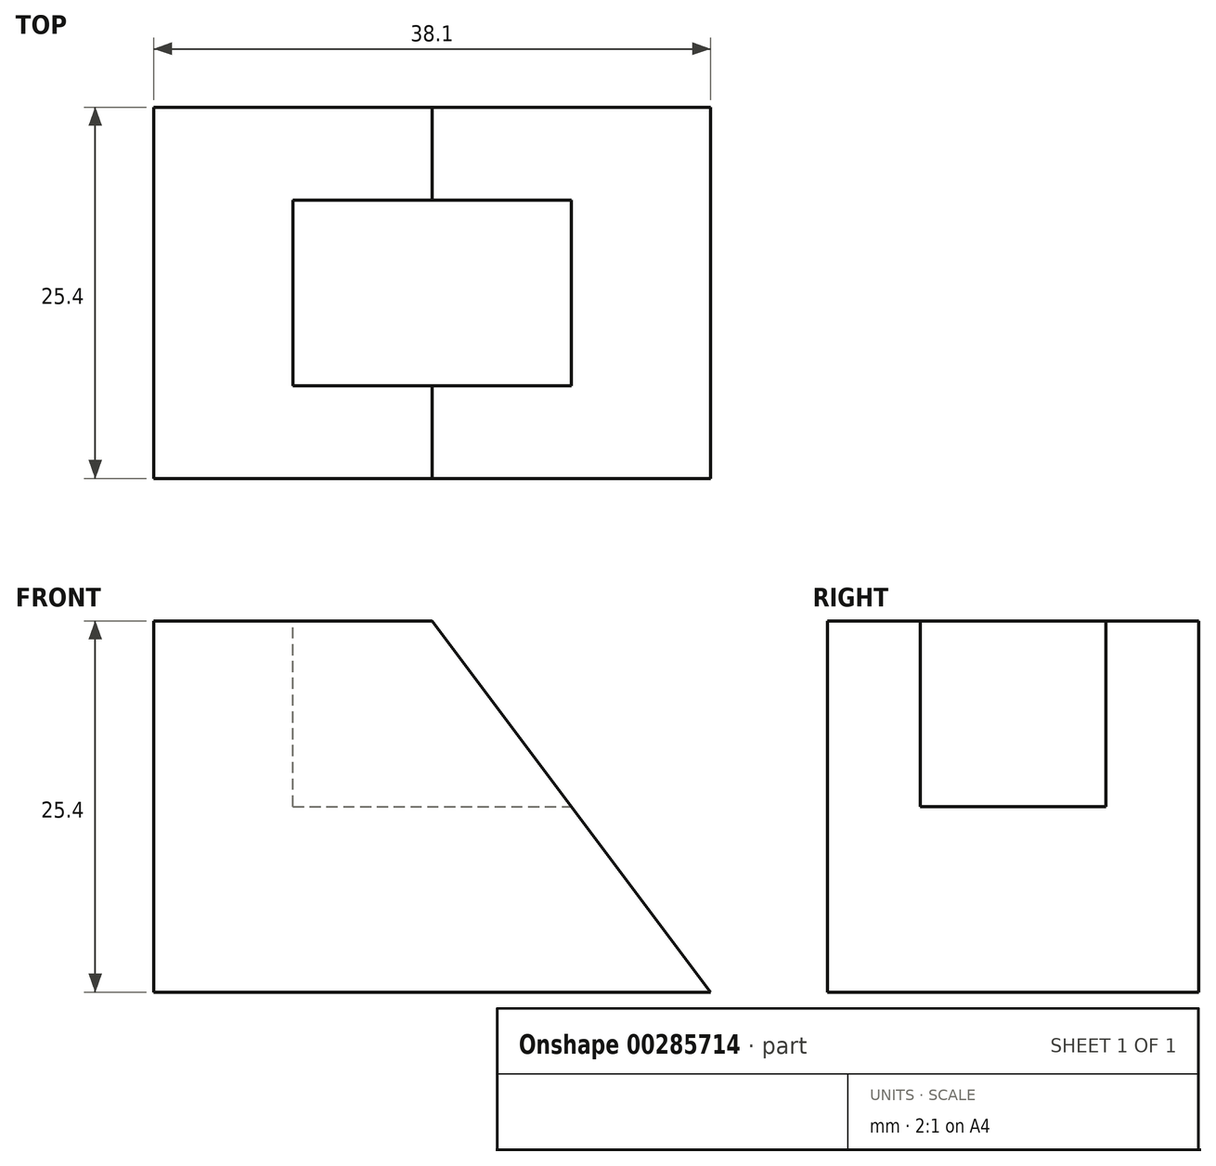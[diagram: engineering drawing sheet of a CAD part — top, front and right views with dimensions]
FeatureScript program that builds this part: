
annotation { "Feature Type Name" : "Feature", "Feature Type Description" : "" }
export const myFeature = defineFeature(function(context is Context, id is Id, definition is map)
    precondition{}
    {
        {
            var Q0;
            Q0=qCreatedBy(makeId("Front.planeOp"),FACE);
            var sketch = newSketch(context, id + "F0", { "sketchPlane" : qUnion([Q0])});
            skLineSegment(sketch, "E0", {"start": v(0, 0) * mm, "end": v(0, 25.4) * mm});
            skLineSegment(sketch, "E1", {"start": v(0, 25.4) * mm, "end": v(19.05, 25.4) * mm});
            skLineSegment(sketch, "E2", {"start": v(19.05, 25.4) * mm, "end": v(38.1, 0) * mm});
            skLineSegment(sketch, "E3", {"start": v(0, 0) * mm, "end": v(38.1, 0) * mm});
            skSolve(sketch);
        }
        {
            var Q0;
            Q0 = qSketchRegion(id + "F0", true);
            extrude(context, id + "F1", {"entities" : qUnion([Q0]), "endBound" : BoundingType.SYMMETRIC, "depth" : 25.4 * mm});
        }
        {
            var Q0;
            Q0=makeQuery(id+"F1.opExtrude","SWEPT_FACE",FACE,{"disambiguationData":[OSD([sQuery(id+"F0.wireOp",EDGE,"E1")])]});
            var sketch = newSketch(context, id + "F2", { "sketchPlane" : qUnion([Q0])});
            skLineSegment(sketch, "E4.bottom", {"start": v(9.52, -6.35) * mm, "end": v(38.1, -6.35) * mm});
            skLineSegment(sketch, "E4.top", {"start": v(9.52, 6.35) * mm, "end": v(38.1, 6.35) * mm});
            skLineSegment(sketch, "E4.left", {"start": v(9.53, -6.35) * mm, "end": v(9.53, 6.35) * mm});
            skLineSegment(sketch, "E4.right", {"start": v(38.1, -6.35) * mm, "end": v(38.1, 6.35) * mm});
            skSolve(sketch);
        }
        {
            var Q0;
            Q0 = qSketchRegion(id + "F2", true);
            extrude(context, id + "F3", {"entities" : qUnion([Q0]), "operationType" : NewBodyOperationType.REMOVE, "oppositeDirection" : true, "depth" : 12.7 * mm});
        }
    });
